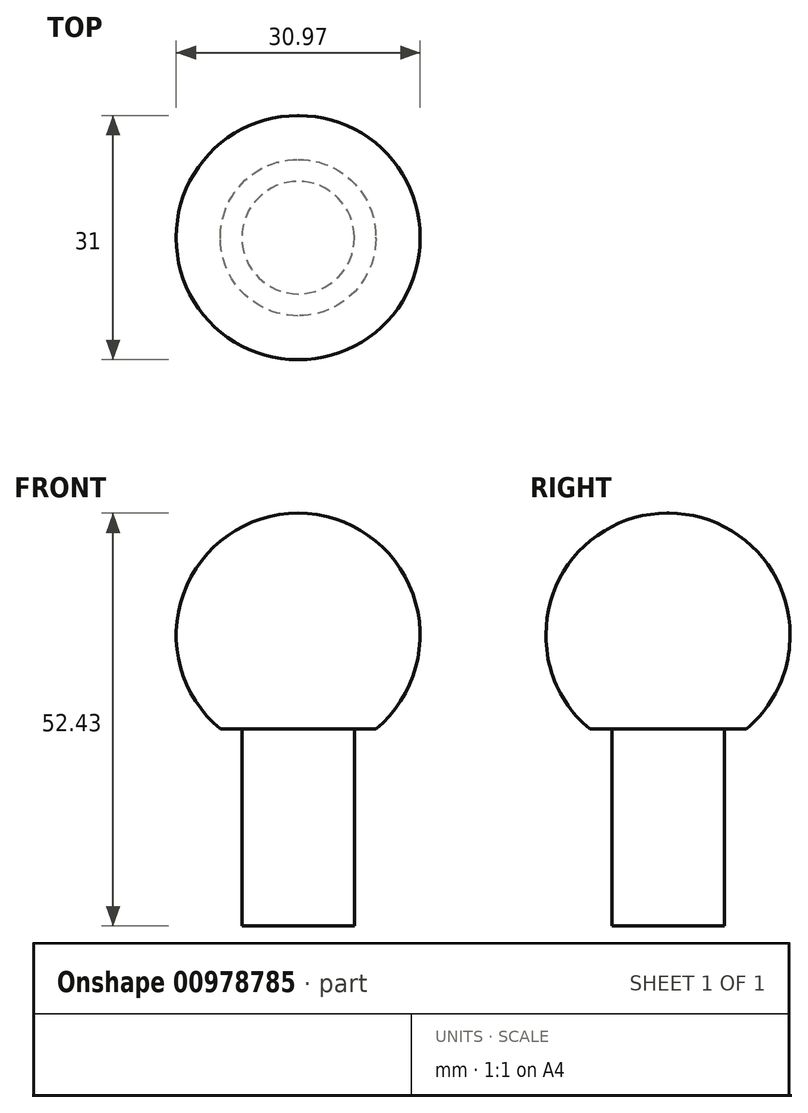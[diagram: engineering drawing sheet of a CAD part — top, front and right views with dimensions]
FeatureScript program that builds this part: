
annotation { "Feature Type Name" : "Feature", "Feature Type Description" : "" }
export const myFeature = defineFeature(function(context is Context, id is Id, definition is map)
    precondition{}
    {
        {
            var Q0;
            Q0=qCreatedBy(makeId("Top.planeOp"),FACE);
            var sketch = newSketch(context, id + "F0", { "sketchPlane" : qUnion([Q0])});
            skCircle(sketch, "E0", {"center": v(0, 0) * mm, "radius": 7.15 * mm});
            skSolve(sketch);
        }
        {
            var Q0;
            Q0=makeQuery(id+"F0.imprint","IMPRINT",FACE,{"disambiguationData":[TD([[makeQuery(id+"F0.imprint","IMPRINT",EDGE,{"derivedFrom":sQuery(id+"F0.wireOp",EDGE,"E0")}),1.0]])]});
            extrude(context, id + "F1", {"entities" : qUnion([Q0]), "oppositeDirection" : true, "depth" : 25 * mm, "offsetDistance" : 25 * mm});
        }
        {
            var Q0;
            Q0=qCreatedBy(makeId("Front.planeOp"),FACE);
            var sketch = newSketch(context, id + "F2", { "sketchPlane" : qUnion([Q0])});
            skArc(sketch, "E1", {"start": v(9.86, 0) * mm, "mid": v(0, 27.43) * mm, "end": v(-9.87, 0) * mm});
            skPoint(sketch, "E1.first.point", {"position": v(-9.87, 0) * mm});
            skPoint(sketch, "E1.second.point", {"position": v(9.86, 0) * mm});
            skPoint(sketch, "E1.third.point", {"position": v(0, 27.43) * mm});
            skLineSegment(sketch, "E2", {"start": v(-9.87, 0) * mm, "end": v(9.86, 0) * mm});
            skSolve(sketch);
        }
        {
            var Q0;
            Q0=makeQuery(id+"F2.imprint","IMPRINT",FACE,{"disambiguationData":[TD([[makeQuery(id+"F2.imprint","IMPRINT",EDGE,{"derivedFrom":sQuery(id+"F2.wireOp",EDGE,"E1")}),1.0]])]});
            extrude(context, id + "F3", {"entities" : qUnion([Q0]), "operationType" : NewBodyOperationType.ADD, "endBound" : BoundingType.SYMMETRIC, "depth" : 31 * mm, "offsetDistance" : 25 * mm});
        }
        {
            var Q0;
            Q0=makeQuery(id+"F3.opExtrude","CAP_EDGE",EDGE,{"disambiguationData":[OSD([sQuery(id+"F2.wireOp",EDGE,"E1")])],"isStart":false});
            fillet(context, id + "F4", {"entities" : qUnion([Q0]), "radius" : 15.4 * mm, "tangentPropagation" : true, "allowEdgeOverflow" : false});
        }
        {
            var Q0;
            Q0=makeQuery(id+"F3.opExtrude","CAP_EDGE",EDGE,{"disambiguationData":[OSD([sQuery(id+"F2.wireOp",EDGE,"E1")])],"isStart":true});
            fillet(context, id + "F5", {"entities" : qUnion([Q0]), "radius" : 15.4 * mm, "tangentPropagation" : true, "allowEdgeOverflow" : false});
        }
    });
